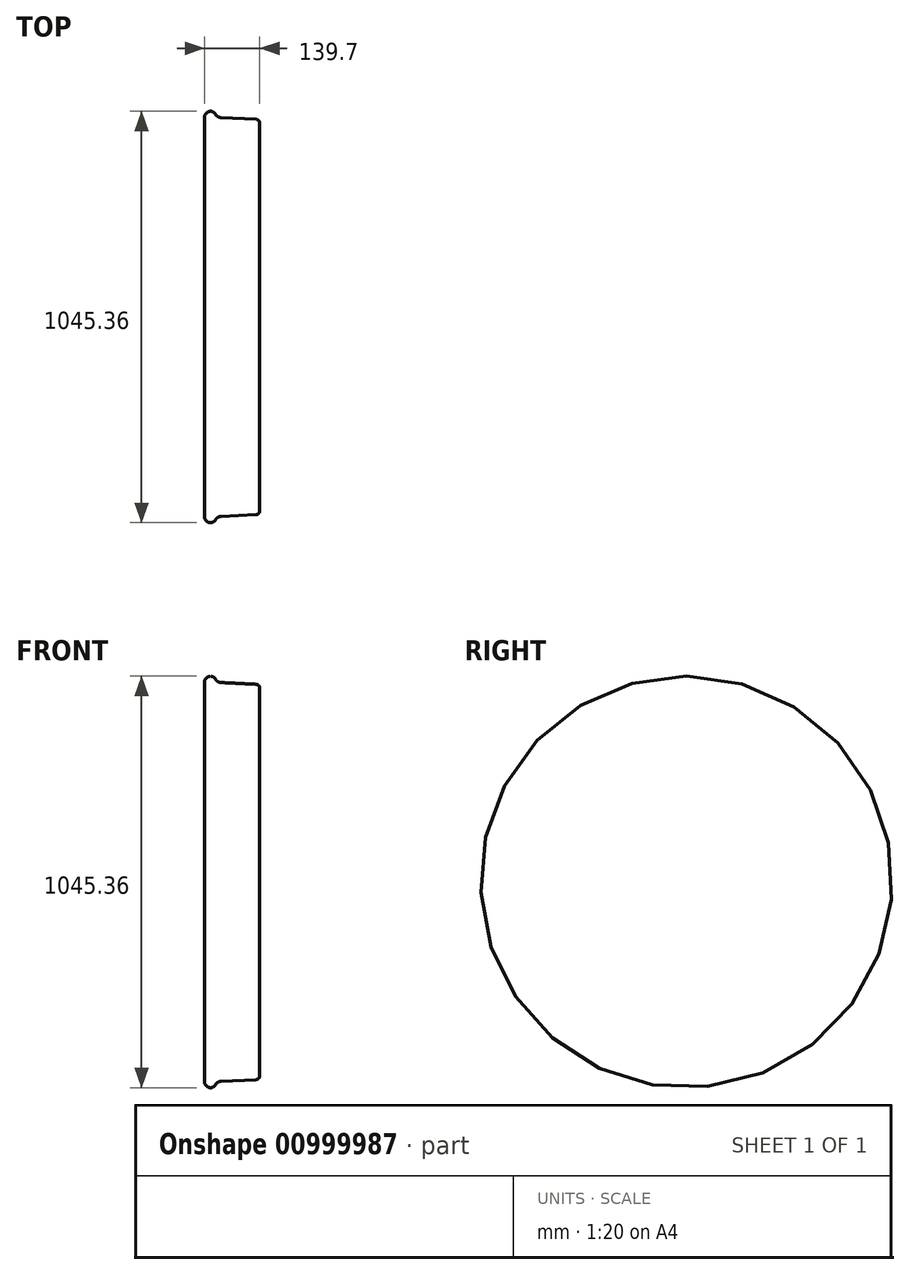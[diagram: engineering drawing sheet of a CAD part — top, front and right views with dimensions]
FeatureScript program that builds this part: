
annotation { "Feature Type Name" : "Feature", "Feature Type Description" : "" }
export const myFeature = defineFeature(function(context is Context, id is Id, definition is map)
    precondition{}
    {
        {
            var Q0;
            Q0=qCreatedBy(makeId("Front.planeOp"),FACE);
            var sketch = newSketch(context, id + "F0", { "sketchPlane" : qUnion([Q0])});
            skCircle(sketch, "E0", {"center": v(0, -508) * mm, "radius": 14.68 * mm});
            skLineSegment(sketch, "E1", {"start": v(14.68, -508) * mm, "end": v(125.02, -508) * mm, "construction": true});
            skLineSegment(sketch, "E2", {"start": v(0, -508) * mm, "end": v(125.02, -501.81) * mm});
            skLineSegment(sketch, "E3", {"start": v(125.02, -501.81) * mm, "end": v(125.02, 0) * mm});
            skLineSegment(sketch, "E4", {"start": v(-14.68, -508) * mm, "end": v(-14.68, 0) * mm});
            skLineSegment(sketch, "E5", {"start": v(-14.68, 0) * mm, "end": v(125.02, 0) * mm});
            skSolve(sketch);
        }
        {
            var Q0;
            {var subQ0=sQuery(id+"F0.wireOp",EDGE,"E0");var subQ1=makeQuery(id+"F0.imprint","INTERSECT",VERTEX,{"derivedFrom":[subQ0,sQuery(id+"F0.wireOp",EDGE,"E4")]});Q0=makeQuery(id+"F0.imprint","IMPRINT",FACE,{"disambiguationData":[TD([[makeQuery(id+"F0.imprint","IMPRINT",EDGE,{"disambiguationData":[TD([[subQ1,1.0]])],"derivedFrom":subQ0}),1.0]])]});}
            var Q1;
            {var subQ1=sQuery(id+"F0.wireOp",EDGE,"E3");Q1=makeQuery(id+"F0.imprint","IMPRINT",FACE,{"disambiguationData":[TD([[makeQuery(id+"F0.imprint","IMPRINT",EDGE,{"derivedFrom":subQ1}),1.0]])]});}
            var Q2;
            Q2=sQuery(id+"F0.wireOp",EDGE,"E5");
            revolve(context, id + "F1", {"surfaceOperationType" : NewSurfaceOperationType.NEW, "entities" : qUnion([Q0, Q1]), "axis" : qUnion([Q2]), "revolveType" : RevolveType.FULL});
        }
        {
            var Q0;
            Q0=makeQuery(id+"F1.opRevolve","SWEPT_EDGE",EDGE,{"disambiguationData":[OSD([sQuery(id+"F0.wireOp",EDGE,"E0"),sQuery(id+"F0.wireOp",EDGE,"E2")])]});
            fillet(context, id + "F2", {"entities" : qUnion([Q0]), "radius" : 17.48 * mm, "tangentPropagation" : true, "allowEdgeOverflow" : false});
        }
        {
            var Q0;
            Q0=makeQuery(id+"F1.opRevolve","SWEPT_EDGE",EDGE,{"disambiguationData":[OSD([sQuery(id+"F0.wireOp",EDGE,"E2"),sQuery(id+"F0.wireOp",EDGE,"E3")])]});
            fillet(context, id + "F3", {"entities" : qUnion([Q0]), "radius" : 9.52 * mm, "tangentPropagation" : true, "allowEdgeOverflow" : false});
        }
    });
